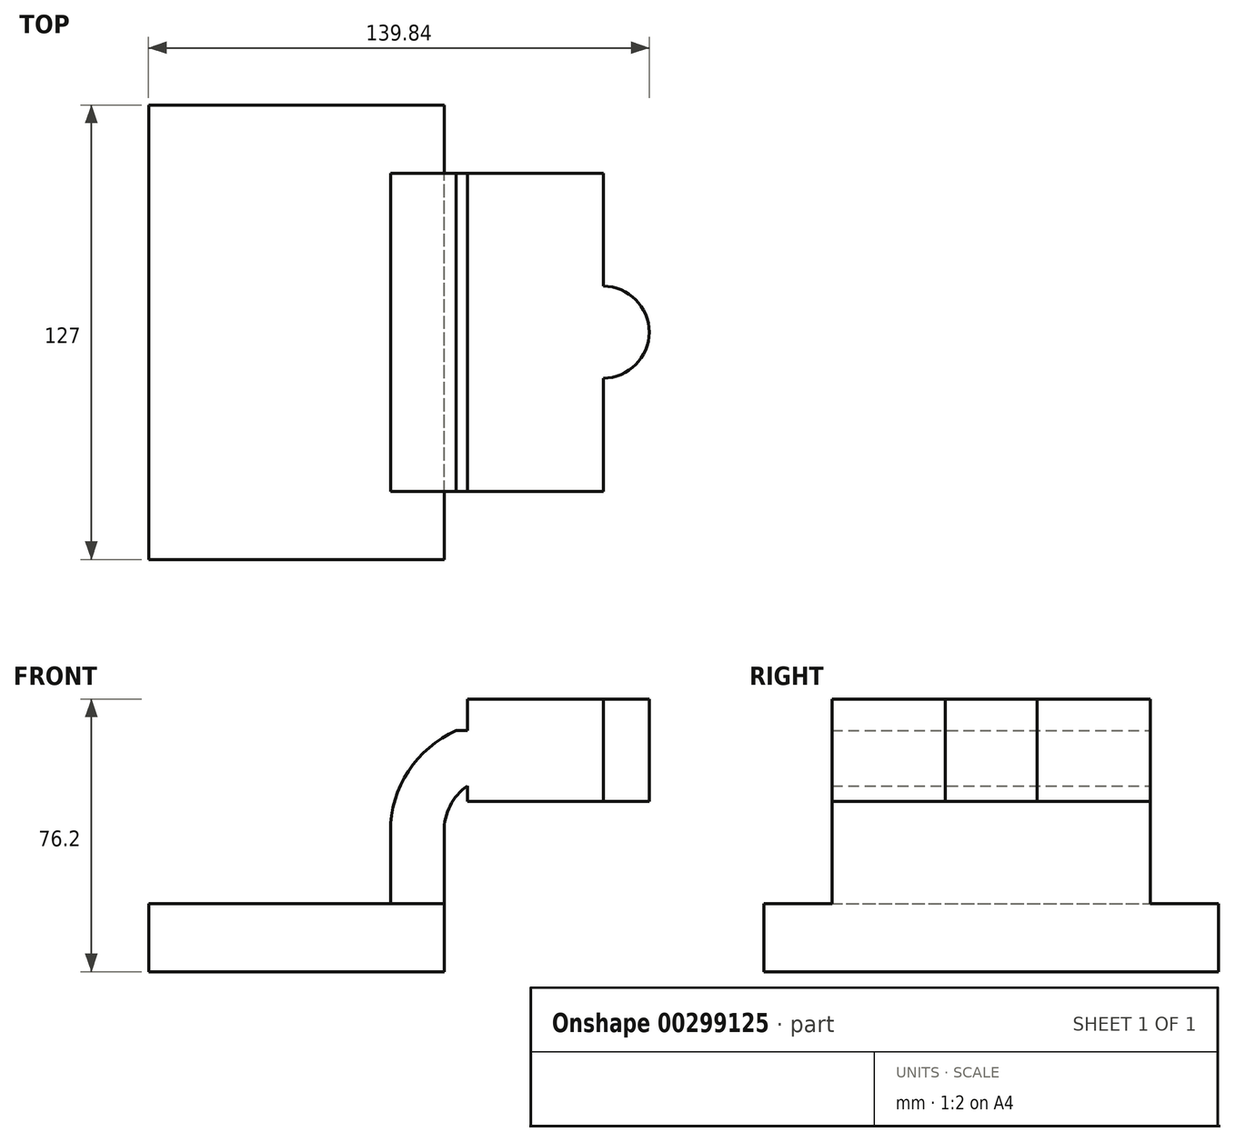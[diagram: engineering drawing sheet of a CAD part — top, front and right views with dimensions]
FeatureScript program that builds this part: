
annotation { "Feature Type Name" : "Feature", "Feature Type Description" : "" }
export const myFeature = defineFeature(function(context is Context, id is Id, definition is map)
    precondition{}
    {
        {
            var Q0;
            Q0=qCreatedBy(makeId("Front.planeOp"),FACE);
            var sketch = newSketch(context, id + "F0", { "sketchPlane" : qUnion([Q0])});
            skLineSegment(sketch, "E0.bottom", {"start": v(-30.6, 4.26) * mm, "end": v(51.94, 4.26) * mm});
            skLineSegment(sketch, "E0.top", {"start": v(-30.6, -14.79) * mm, "end": v(51.94, -14.79) * mm});
            skLineSegment(sketch, "E0.left", {"start": v(-30.6, 4.26) * mm, "end": v(-30.6, -14.79) * mm});
            skLineSegment(sketch, "E0.right", {"start": v(51.94, 4.26) * mm, "end": v(51.94, -14.79) * mm});
            skLineSegment(sketch, "E1.bottom", {"start": v(58.43, 61.41) * mm, "end": v(109.23, 61.41) * mm});
            skLineSegment(sketch, "E1.top", {"start": v(58.43, 32.84) * mm, "end": v(109.23, 32.84) * mm});
            skLineSegment(sketch, "E1.left", {"start": v(58.43, 61.41) * mm, "end": v(58.43, 32.84) * mm});
            skLineSegment(sketch, "E1.right", {"start": v(109.23, 61.41) * mm, "end": v(109.23, 32.84) * mm});
            skLineSegment(sketch, "E2", {"start": v(51.94, 4.26) * mm, "end": v(51.94, 24.36) * mm});
            skArc(sketch, "E3", {"start": v(51.94, 24.36) * mm, "mid": v(53.84, 31.89) * mm, "end": v(59.08, 37.61) * mm});
            skLineSegment(sketch, "E4", {"start": v(59.08, 37.61) * mm, "end": v(96.4, 37.61) * mm});
            skLineSegment(sketch, "E5.0", {"start": v(55.37, 52.6) * mm, "end": v(96.4, 52.6) * mm});
            skArc(sketch, "E5.1", {"start": v(36.96, 24.36) * mm, "mid": v(41.97, 41.22) * mm, "end": v(55.37, 52.6) * mm});
            skLineSegment(sketch, "E5.2", {"start": v(36.96, 4.26) * mm, "end": v(36.96, 24.36) * mm});
            skLineSegment(sketch, "E6", {"start": v(96.4, 37.61) * mm, "end": v(96.4, 52.6) * mm});
            skLineSegment(sketch, "E7", {"start": v(96.4, 52.6) * mm, "end": v(96.4, 61.41) * mm});
            skLineSegment(sketch, "E8", {"start": v(96.4, 61.41) * mm, "end": v(96.4, 37.61) * mm});
            skLineSegment(sketch, "E9", {"start": v(96.4, 37.61) * mm, "end": v(96.4, 32.84) * mm});
            skFitSpline(sketch, "E10", {"points": [v(-30.6, 4.26) * mm, v(55.37, 52.6) * mm], "startDerivative": vector(1.87, 96.01) * mm, "endDerivative": vector(133.56, -0.7) * mm});
            skSolve(sketch);
        }
        {
            var Q0;
            Q0=makeQuery(id+"F0.imprint","IMPRINT",FACE,{"disambiguationData":[TD([[makeQuery(id+"F0.imprint","IMPRINT",EDGE,{"derivedFrom":sQuery(id+"F0.wireOp",EDGE,"E0.top")}),1.0]])]});
            extrude(context, id + "F1", {"entities" : qUnion([Q0]), "endBound" : BoundingType.SYMMETRIC, "depth" : 127 * mm});
        }
        {
            var Q0;
            Q0=makeQuery(id+"F0.imprint","IMPRINT",FACE,{"disambiguationData":[TD([[makeQuery(id+"F0.imprint","IMPRINT",EDGE,{"derivedFrom":sQuery(id+"F0.wireOp",EDGE,"E5.1")}),1.0]])]});
            extrude(context, id + "F2", {"entities" : qUnion([Q0]), "operationType" : NewBodyOperationType.ADD, "endBound" : BoundingType.SYMMETRIC, "depth" : 50.8 * mm});
        }
        {
            var Q0;
            {var subQ1=sQuery(id+"F0.wireOp",EDGE,"E2");Q0=makeQuery(id+"F0.imprint","IMPRINT",FACE,{"disambiguationData":[TD([[makeQuery(id+"F0.imprint","IMPRINT",EDGE,{"derivedFrom":subQ1}),1.0]])]});}
            var Q1;
            {var subQ5=sQuery(id+"F0.wireOp",EDGE,"E4");Q1=makeQuery(id+"F0.imprint","IMPRINT",FACE,{"disambiguationData":[TD([[makeQuery(id+"F0.imprint","IMPRINT",EDGE,{"derivedFrom":subQ5}),1.0]])]});}
            var Q2;
            {var subQ0=sQuery(id+"F0.wireOp",EDGE,"E4");Q2=makeQuery(id+"F0.imprint","IMPRINT",FACE,{"disambiguationData":[TD([[makeQuery(id+"F0.imprint","IMPRINT",EDGE,{"derivedFrom":subQ0}),-1.0]])]});}
            var Q3;
            {var subQ0=sQuery(id+"F0.wireOp",EDGE,"E1.left");var subQ1=sQuery(id+"F0.wireOp",EDGE,"E1.bottom");var subQ2=makeQuery(id+"F0.imprint","INTERSECT",VERTEX,{"derivedFrom":[subQ1,subQ0]});Q3=makeQuery(id+"F0.imprint","IMPRINT",FACE,{"disambiguationData":[TD([[makeQuery(id+"F0.imprint","IMPRINT",EDGE,{"disambiguationData":[TD([[subQ2,-1.0]])],"derivedFrom":subQ1}),-1.0]])]});}
            extrude(context, id + "F3", {"entities" : qUnion([Q0, Q1, Q2, Q3]), "operationType" : NewBodyOperationType.ADD, "endBound" : BoundingType.SYMMETRIC, "depth" : 88.9 * mm});
        }
        {
            var Q0;
            {var subQ0=sQuery(id+"F0.wireOp",EDGE,"E1.right");Q0=makeQuery(id+"F0.imprint","IMPRINT",FACE,{"disambiguationData":[TD([[makeQuery(id+"F0.imprint","IMPRINT",EDGE,{"derivedFrom":subQ0}),-1.0]])]});}
            var Q1;
            Q1=sQuery(id+"F0.wireOp",EDGE,"E8");
            revolve(context, id + "F4", {"operationType" : NewBodyOperationType.ADD, "entities" : qUnion([Q0]), "axis" : qUnion([Q1]), "revolveType" : RevolveType.FULL});
        }
    });
